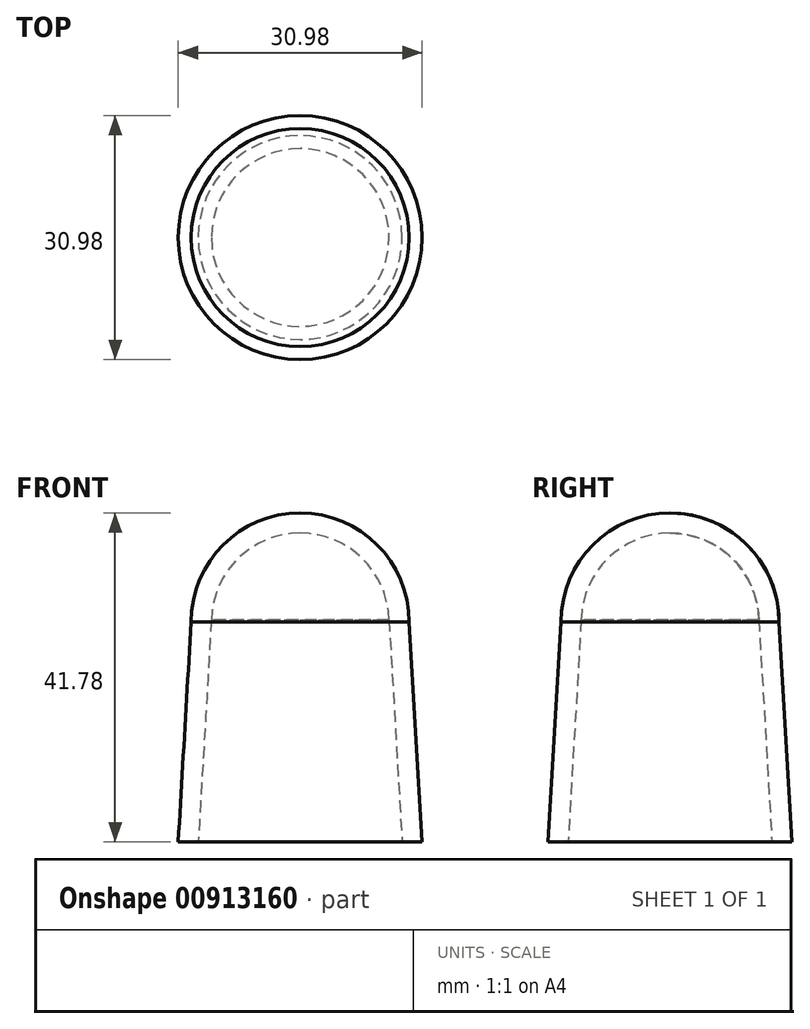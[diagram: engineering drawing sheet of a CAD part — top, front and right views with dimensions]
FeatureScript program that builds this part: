
annotation { "Feature Type Name" : "Feature", "Feature Type Description" : "" }
export const myFeature = defineFeature(function(context is Context, id is Id, definition is map)
    precondition{}
    {
        {
            var Q0;
            Q0=qCreatedBy(makeId("Right.planeOp"),FACE);
            var sketch = newSketch(context, id + "F0", { "sketchPlane" : qUnion([Q0])});
            skLineSegment(sketch, "E0", {"start": v(-2.15, -26.88) * mm, "end": v(-2.15, -26.88) * mm});
            skLineSegment(sketch, "E1", {"start": v(15.5, 0) * mm, "end": v(13.84, 27.94) * mm});
            skArc(sketch, "E2", {"start": v(13.84, 27.94) * mm, "mid": v(9.79, 37.73) * mm, "end": v(0, 41.78) * mm});
            skArc(sketch, "E3", {"start": v(11.28, 28.2) * mm, "mid": v(7.89, 36.01) * mm, "end": v(0, 39.23) * mm});
            skLineSegment(sketch, "E4", {"start": v(12.95, 0) * mm, "end": v(11.28, 28.2) * mm});
            skLineSegment(sketch, "E5", {"start": v(12.95, 0) * mm, "end": v(12.95, 0) * mm});
            skLineSegment(sketch, "E6", {"start": v(0, 0) * mm, "end": v(0, 41.78) * mm});
            skLineSegment(sketch, "E7", {"start": v(12.95, 0) * mm, "end": v(15.5, 0) * mm});
            skSolve(sketch);
        }
        {
            var Q0;
            Q0=makeQuery(id+"F0.imprint","IMPRINT",FACE,{"disambiguationData":[TD([[makeQuery(id+"F0.imprint","IMPRINT",EDGE,{"derivedFrom":sQuery(id+"F0.wireOp",EDGE,"E1")}),1.0]])]});
            var Q1;
            Q1=sQuery(id+"F0.wireOp",EDGE,"E6");
            revolve(context, id + "F1", {"surfaceOperationType" : NewSurfaceOperationType.NEW, "entities" : qUnion([Q0]), "axis" : qUnion([Q1]), "revolveType" : RevolveType.FULL});
        }
    });
